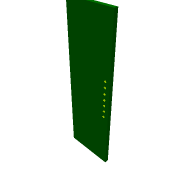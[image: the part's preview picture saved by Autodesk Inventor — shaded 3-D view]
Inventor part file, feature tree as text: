
AUTODESK INVENTOR PART (.ipt)
format: ipt  version: 2016 (Build 200138000, 138)  size: 116,736 bytes
history: native  units: mm
features: sketch x8, extrude x1, other x1
ambient origin geometry x8: Origin, YZ Plane, XZ Plane, XY Plane, X Axis, Y Axis, Z Axis, Center Point
bodies: Body1 (feature_tree)
feature tree (10):
  extrude  "Extrusion3"  Depth=63.5mm
  sketch  "Sketch2"  dims[d4=1.0mm]
  sketch  "Sketch3"  dims[d5=1.0mm]
  sketch  "Sketch4"  dims[d6=1.0mm]
  sketch  "Sketch5"  dims[d7=1.0mm]
  sketch  "Sketch6"  dims[d8=1.0mm]
  sketch  "Sketch7"  dims[d9=1.0mm]
  sketch  "Sketch8"  dims[d10=2.54mm d11=2.54mm d12=2.54mm d13=2.54mm d14=2.54mm d19=2.0mm d20=1.0mm d21=2.54mm d22=31.75mm d23=1.6mm d24=0.0mm]
  other  "GND"
  sketch  "Sketch1"  dims[d0=19.685mm d1=63.5mm]
